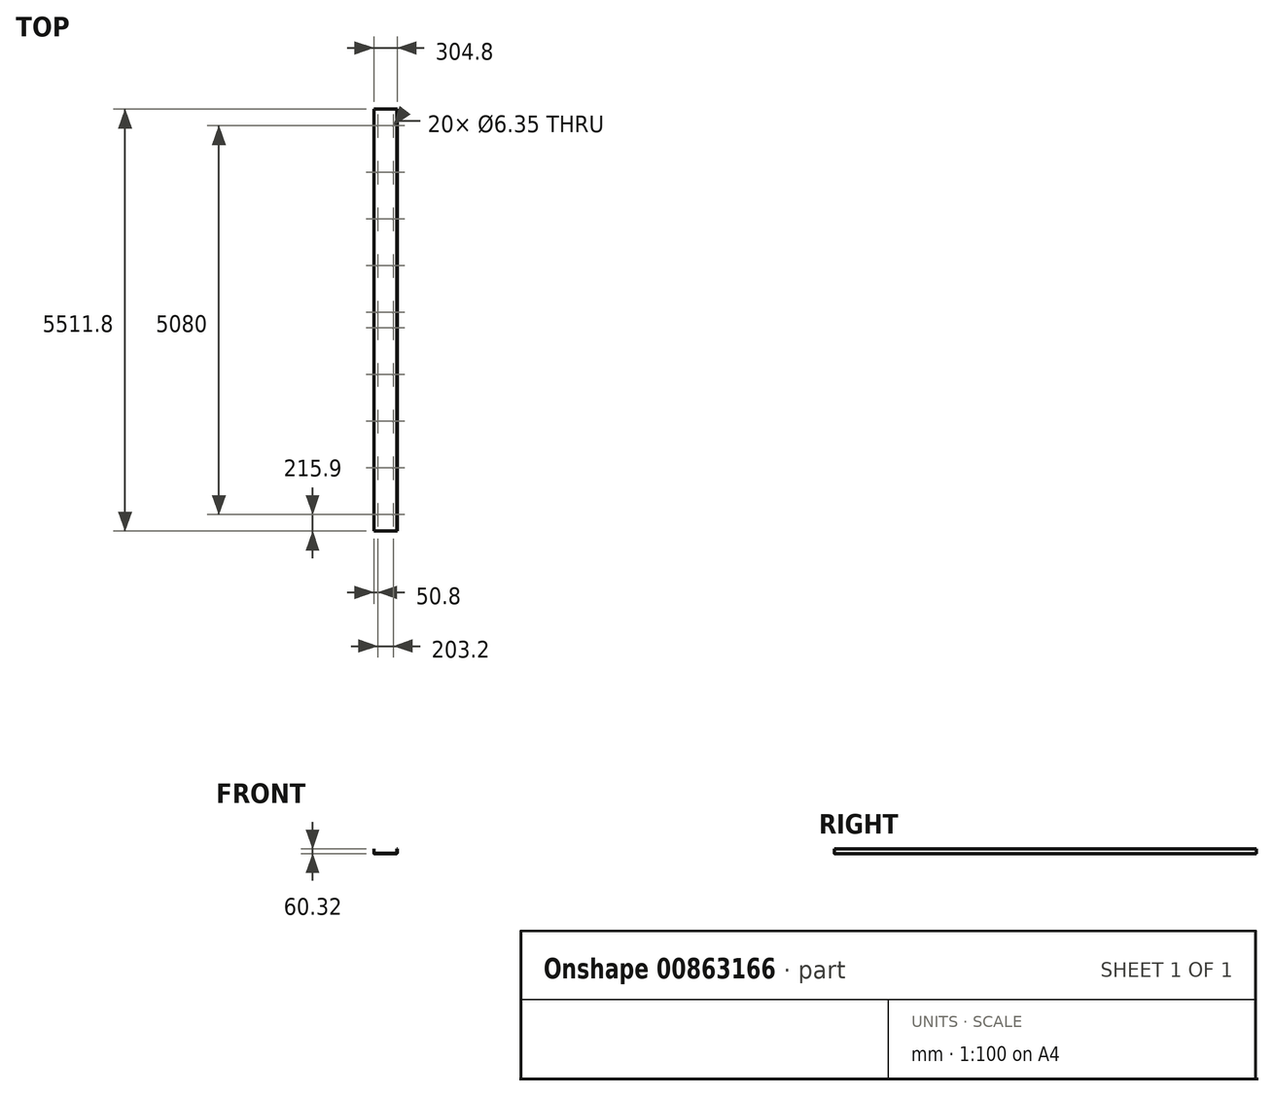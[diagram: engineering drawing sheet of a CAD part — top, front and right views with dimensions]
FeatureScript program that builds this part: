
annotation { "Feature Type Name" : "Feature", "Feature Type Description" : "" }
export const myFeature = defineFeature(function(context is Context, id is Id, definition is map)
    precondition{}
    {
        {
            var Q0;
            Q0=qCreatedBy(makeId("Top.planeOp"),FACE);
            var sketch = newSketch(context, id + "F0", { "sketchPlane" : qUnion([Q0])});
            skLineSegment(sketch, "E0.bottom", {"start": v(-152.4, -2819.4) * mm, "end": v(152.4, -2819.4) * mm});
            skLineSegment(sketch, "E0.top", {"start": v(-152.4, 2819.4) * mm, "end": v(152.4, 2819.4) * mm});
            skLineSegment(sketch, "E0.left", {"start": v(-152.4, -2819.4) * mm, "end": v(-152.4, 2819.4) * mm});
            skLineSegment(sketch, "E0.right", {"start": v(152.4, -2819.4) * mm, "end": v(152.4, 2819.4) * mm});
            skPoint(sketch, "E0.middle", {"position": v(0, 0) * mm});
            skSolve(sketch);
        }
        {
            var Q0;
            Q0 = qSketchRegion(id + "F0", true);
            extrude(context, id + "F1", {"entities" : qUnion([Q0]), "depth" : 3.17 * mm, "offsetDistance" : 25.4 * mm});
        }
        {
            var Q0;
            Q0=makeQuery(id+"F1.opExtrude","CAP_FACE",FACE,{"disambiguationData":[OSD([sQuery(id+"F0.wireOp",EDGE,"E0.bottom"),sQuery(id+"F0.wireOp",EDGE,"E0.top"),sQuery(id+"F0.wireOp",EDGE,"E0.left"),sQuery(id+"F0.wireOp",EDGE,"E0.right")])],"isStart":false});
            var sketch = newSketch(context, id + "F2", { "sketchPlane" : qUnion([Q0])});
            skLineSegment(sketch, "E1.bottom", {"start": v(152.4, 2819.4) * mm, "end": v(149.22, 2819.4) * mm});
            skLineSegment(sketch, "E1.top", {"start": v(152.4, -2819.4) * mm, "end": v(149.23, -2819.4) * mm});
            skLineSegment(sketch, "E1.left", {"start": v(152.4, 2819.4) * mm, "end": v(152.4, -2819.4) * mm});
            skLineSegment(sketch, "E1.right", {"start": v(149.22, 2819.4) * mm, "end": v(149.23, -2819.4) * mm});
            skSolve(sketch);
        }
        {
            var Q0;
            Q0=makeQuery(id+"F2.imprint","IMPRINT",FACE,{"disambiguationData":[TD([[makeQuery(id+"F2.imprint","IMPRINT",EDGE,{"derivedFrom":sQuery(id+"F2.wireOp",EDGE,"E1.bottom")}),-1.0]])]});
            extrude(context, id + "F3", {"entities" : qUnion([Q0]), "operationType" : NewBodyOperationType.ADD, "depth" : 57.15 * mm, "offsetDistance" : 25.4 * mm});
        }
        {
            var Q0;
            Q0=makeQuery(id+"F1.opExtrude","CAP_FACE",FACE,{"disambiguationData":[OSD([sQuery(id+"F0.wireOp",EDGE,"E0.bottom"),sQuery(id+"F0.wireOp",EDGE,"E0.top"),sQuery(id+"F0.wireOp",EDGE,"E0.left"),sQuery(id+"F0.wireOp",EDGE,"E0.right")])],"isStart":false});
            var sketch = newSketch(context, id + "F4", { "sketchPlane" : qUnion([Q0])});
            skLineSegment(sketch, "E2.bottom", {"start": v(-152.4, 2819.4) * mm, "end": v(-149.23, 2819.4) * mm});
            skLineSegment(sketch, "E2.top", {"start": v(-152.4, -2819.4) * mm, "end": v(-149.22, -2819.4) * mm});
            skLineSegment(sketch, "E2.left", {"start": v(-152.4, 2819.4) * mm, "end": v(-152.4, -2819.4) * mm});
            skLineSegment(sketch, "E2.right", {"start": v(-149.23, 2819.4) * mm, "end": v(-149.22, -2819.4) * mm});
            skSolve(sketch);
        }
        {
            var Q0;
            Q0=makeQuery(id+"F4.imprint","IMPRINT",FACE,{"disambiguationData":[TD([[makeQuery(id+"F4.imprint","IMPRINT",EDGE,{"derivedFrom":sQuery(id+"F4.wireOp",EDGE,"E2.bottom")}),-1.0]])]});
            extrude(context, id + "F5", {"entities" : qUnion([Q0]), "operationType" : NewBodyOperationType.ADD, "depth" : 57.15 * mm, "offsetDistance" : 25.4 * mm});
        }
        {
            var Q0;
            Q0=makeQuery(id+"F5.opExtrude","CAP_EDGE",EDGE,{"disambiguationData":[OSD([sQuery(id+"F4.wireOp",EDGE,"E2.right")])],"isStart":true});
            var Q1;
            Q1=makeQuery(id+"F1.opExtrude","CAP_EDGE",EDGE,{"disambiguationData":[OSD([sQuery(id+"F0.wireOp",EDGE,"E0.right")])],"isStart":true});
            fillet(context, id + "F6", {"entities" : qUnion([Q0, Q1]), "radius" : 3.17 * mm, "tangentPropagation" : true, "allowEdgeOverflow" : false});
        }
        {
            var Q0;
            Q0=makeQuery(id+"F3.opExtrude","CAP_EDGE",EDGE,{"disambiguationData":[OSD([sQuery(id+"F2.wireOp",EDGE,"E1.right")])],"isStart":true});
            var Q1;
            Q1=makeQuery(id+"F1.opExtrude","CAP_EDGE",EDGE,{"disambiguationData":[OSD([sQuery(id+"F0.wireOp",EDGE,"E0.left")])],"isStart":true});
            fillet(context, id + "F7", {"entities" : qUnion([Q0, Q1]), "radius" : 3.17 * mm, "tangentPropagation" : true, "allowEdgeOverflow" : false});
        }
        {
            var Q0;
            Q0=makeQuery(id+"F5.boolean.opBoolean","MERGE",FACE,{"derivedFrom":[makeQuery(id+"F3.boolean.opBoolean","MERGE",FACE,{"derivedFrom":[makeQuery(id+"F1.opExtrude","SWEPT_FACE",FACE,{"disambiguationData":[OSD([sQuery(id+"F0.wireOp",EDGE,"E0.bottom")])]}),makeQuery(id+"F3.opExtrude","SWEPT_FACE",FACE,{"disambiguationData":[OSD([sQuery(id+"F2.wireOp",EDGE,"E1.top")])]})]}),makeQuery(id+"F5.opExtrude","SWEPT_FACE",FACE,{"disambiguationData":[OSD([sQuery(id+"F4.wireOp",EDGE,"E2.top")])]})]});
            extrude(context, id + "F8", {"entities" : qUnion([Q0]), "operationType" : NewBodyOperationType.REMOVE, "oppositeDirection" : true, "depth" : 127 * mm, "offsetDistance" : 25.4 * mm});
        }
        {
            var Q0;
            Q0=makeQuery(id+"F1.opExtrude","CAP_FACE",FACE,{"disambiguationData":[OSD([sQuery(id+"F0.wireOp",EDGE,"E0.bottom"),sQuery(id+"F0.wireOp",EDGE,"E0.top"),sQuery(id+"F0.wireOp",EDGE,"E0.left"),sQuery(id+"F0.wireOp",EDGE,"E0.right")])],"isStart":false});
            var sketch = newSketch(context, id + "F9", { "sketchPlane" : qUnion([Q0])});
            skLineSegment(sketch, "E3", {"start": v(0, 2819.4) * mm, "end": v(0, 63.5) * mm, "construction": true});
            skLineSegment(sketch, "E4", {"start": v(0, 63.5) * mm, "end": v(0, -2692.4) * mm, "construction": true});
            skSolve(sketch);
        }
        {
            var Q0;
            {var subQ0=sQuery(id+"F0.wireOp",EDGE,"E0.top");Q0=makeQuery(id+"F9.imprint","IMPRINT",FACE,{"disambiguationData":[TD([[makeQuery(id+"F9.imprint","IMPRINT",EDGE,{"derivedFrom":makeQuery(id+"F1.opExtrude","CAP_EDGE",EDGE,{"disambiguationData":[OSD([subQ0])],"isStart":false})}),-1.0]])]});}
            var sketch = newSketch(context, id + "F10", { "sketchPlane" : qUnion([Q0])});
            skLineSegment(sketch, "E5", {"start": v(0, 2820.33) * mm, "end": v(-101.6, 2820.33) * mm, "construction": true});
            skLineSegment(sketch, "E6", {"start": v(-101.6, 2820.33) * mm, "end": v(101.6, 2820.33) * mm, "construction": true});
            skLineSegment(sketch, "E7", {"start": v(101.6, 2820.33) * mm, "end": v(101.6, 2718.73) * mm, "construction": true});
            skLineSegment(sketch, "E8", {"start": v(0, 63.5) * mm, "end": v(101.6, 63.5) * mm, "construction": true});
            skLineSegment(sketch, "E9", {"start": v(101.6, 63.5) * mm, "end": v(101.6, 165.1) * mm, "construction": true});
            skLineSegment(sketch, "E10", {"start": v(101.6, 165.1) * mm, "end": v(-101.6, 165.1) * mm, "construction": true});
            skLineSegment(sketch, "E11", {"start": v(-101.6, 165.1) * mm, "end": v(-101.6, 774.7) * mm, "construction": true});
            skLineSegment(sketch, "E12", {"start": v(-101.6, 774.7) * mm, "end": v(101.6, 774.7) * mm, "construction": true});
            skLineSegment(sketch, "E13", {"start": v(101.6, 774.7) * mm, "end": v(101.6, 1384.3) * mm, "construction": true});
            skLineSegment(sketch, "E14", {"start": v(101.6, 1384.3) * mm, "end": v(-101.6, 1384.3) * mm, "construction": true});
            skLineSegment(sketch, "E15", {"start": v(-101.6, 1384.3) * mm, "end": v(-101.6, 1993.9) * mm, "construction": true});
            skLineSegment(sketch, "E16", {"start": v(-101.6, 1993.9) * mm, "end": v(101.6, 1993.9) * mm, "construction": true});
            skLineSegment(sketch, "E17", {"start": v(101.6, 1993.9) * mm, "end": v(101.6, 2603.5) * mm, "construction": true});
            skLineSegment(sketch, "E18", {"start": v(101.6, 2603.5) * mm, "end": v(-101.6, 2603.5) * mm, "construction": true});
            skSolve(sketch);
        }
        {
            var Q0;
            Q0=sQuery(id+"F10.wireOp",VERTEX,"E18.end");
            var Q1;
            Q1=sQuery(id+"F10.wireOp",VERTEX,"E17.end");
            var Q2;
            Q2=sQuery(id+"F10.wireOp",VERTEX,"E16.end");
            var Q3;
            Q3=sQuery(id+"F10.wireOp",VERTEX,"E15.end");
            var Q4;
            Q4=sQuery(id+"F10.wireOp",VERTEX,"E14.end");
            var Q5;
            Q5=sQuery(id+"F10.wireOp",VERTEX,"E13.end");
            var Q6;
            Q6=sQuery(id+"F10.wireOp",VERTEX,"E12.end");
            var Q7;
            Q7=sQuery(id+"F10.wireOp",VERTEX,"E11.end");
            var Q8;
            Q8=sQuery(id+"F10.wireOp",VERTEX,"E10.end");
            var Q9;
            Q9=sQuery(id+"F10.wireOp",VERTEX,"E9.end");
            var Q10;
            Q10=makeQuery(id+"F1.opExtrude","SWEPT_BODY",BODY,{"disambiguationData":[OSD([sQuery(id+"F0.wireOp",EDGE,"E0.bottom"),sQuery(id+"F0.wireOp",EDGE,"E0.top"),sQuery(id+"F0.wireOp",EDGE,"E0.left"),sQuery(id+"F0.wireOp",EDGE,"E0.right")])]});
            hole(context, id + "F11", {"style" : HoleStyle.SIMPLE, "endStyle" : HoleEndStyle.THROUGH, "holeDiameter" : 6.35 * mm, "majorDiameter" : 6.35 * mm, "isTappedThrough" : true, "tappedDepth" : 12.7 * mm, "tapClearance" : 3, "locations" : qUnion([Q0, Q1, Q2, Q3, Q4, Q5, Q6, Q7, Q8, Q9]), "scope" : qUnion([Q10])});
        }
        {
            var Q0;
            {var subQ0=sQuery(id+"F0.wireOp",EDGE,"E0.top");Q0=makeQuery(id+"F9.imprint","IMPRINT",FACE,{"disambiguationData":[TD([[makeQuery(id+"F9.imprint","IMPRINT",EDGE,{"derivedFrom":makeQuery(id+"F1.opExtrude","CAP_EDGE",EDGE,{"disambiguationData":[OSD([subQ0])],"isStart":false})}),-1.0]])]});}
            var sketch = newSketch(context, id + "F12", { "sketchPlane" : qUnion([Q0])});
            skLineSegment(sketch, "E19", {"start": v(0, 63.5) * mm, "end": v(-101.6, 63.5) * mm, "construction": true});
            skLineSegment(sketch, "E20", {"start": v(-101.6, 63.5) * mm, "end": v(-101.6, -38.1) * mm, "construction": true});
            skLineSegment(sketch, "E21", {"start": v(-101.6, -38.1) * mm, "end": v(101.6, -38.1) * mm, "construction": true});
            skLineSegment(sketch, "E22", {"start": v(101.6, -38.1) * mm, "end": v(101.6, -647.7) * mm, "construction": true});
            skLineSegment(sketch, "E23", {"start": v(101.6, -647.7) * mm, "end": v(-101.6, -647.7) * mm, "construction": true});
            skLineSegment(sketch, "E24", {"start": v(-101.6, -647.7) * mm, "end": v(-101.6, -1257.3) * mm, "construction": true});
            skLineSegment(sketch, "E25", {"start": v(-101.6, -1257.3) * mm, "end": v(101.6, -1257.3) * mm, "construction": true});
            skLineSegment(sketch, "E26", {"start": v(101.6, -1257.3) * mm, "end": v(101.6, -1866.9) * mm, "construction": true});
            skLineSegment(sketch, "E27", {"start": v(101.6, -1866.9) * mm, "end": v(-101.6, -1866.9) * mm, "construction": true});
            skLineSegment(sketch, "E28", {"start": v(-101.6, -1866.9) * mm, "end": v(-101.6, -2476.5) * mm, "construction": true});
            skLineSegment(sketch, "E29", {"start": v(-101.6, -2476.5) * mm, "end": v(101.6, -2476.5) * mm, "construction": true});
            skSolve(sketch);
        }
        {
            var Q0;
            Q0=sQuery(id+"F12.wireOp",VERTEX,"E20.end");
            var Q1;
            Q1=sQuery(id+"F12.wireOp",VERTEX,"E21.end");
            var Q2;
            Q2=sQuery(id+"F12.wireOp",VERTEX,"E22.end");
            var Q3;
            Q3=sQuery(id+"F12.wireOp",VERTEX,"E23.end");
            var Q4;
            Q4=sQuery(id+"F12.wireOp",VERTEX,"E24.end");
            var Q5;
            Q5=sQuery(id+"F12.wireOp",VERTEX,"E25.end");
            var Q6;
            Q6=sQuery(id+"F12.wireOp",VERTEX,"E26.end");
            var Q7;
            Q7=sQuery(id+"F12.wireOp",VERTEX,"E27.end");
            var Q8;
            Q8=sQuery(id+"F12.wireOp",VERTEX,"E28.end");
            var Q9;
            Q9=sQuery(id+"F12.wireOp",VERTEX,"E29.end");
            var Q10;
            Q10=makeQuery(id+"F1.opExtrude","SWEPT_BODY",BODY,{"disambiguationData":[OSD([sQuery(id+"F0.wireOp",EDGE,"E0.bottom"),sQuery(id+"F0.wireOp",EDGE,"E0.top"),sQuery(id+"F0.wireOp",EDGE,"E0.left"),sQuery(id+"F0.wireOp",EDGE,"E0.right")])]});
            hole(context, id + "F13", {"style" : HoleStyle.SIMPLE, "endStyle" : HoleEndStyle.THROUGH, "holeDiameter" : 6.35 * mm, "majorDiameter" : 6.35 * mm, "isTappedThrough" : true, "tappedDepth" : 12.7 * mm, "tapClearance" : 3, "locations" : qUnion([Q0, Q1, Q2, Q3, Q4, Q5, Q6, Q7, Q8, Q9]), "scope" : qUnion([Q10])});
        }
    });
